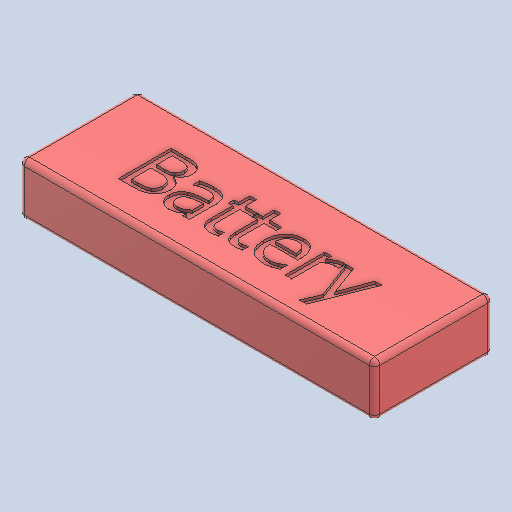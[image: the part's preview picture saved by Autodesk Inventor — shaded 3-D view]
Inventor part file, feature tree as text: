
AUTODESK INVENTOR PART (.ipt)
format: ipt  version: 2023 (Build 270158000, 158)  size: 488,448 bytes
history: native  units: in
note: dims shown in document units (in); Inventor stores cm internally (conversion verified against a paired STEP export)
features: extrude x2, sketch x2, fillet x1
ambient origin geometry x8: Origin, YZ Plane, XZ Plane, XY Plane, X Axis, Y Axis, Z Axis, Center Point
bodies: Solid1 (feature_tree)
feature tree (5):
  extrude  "Extrusion1"  Depth=1.7717in
  extrude  "Extrusion2"  Depth=0.0787in TaperAngle=0.0deg
  fillet  "Fillet1"  Radius=0.0787in
  sketch  "Sketch1"  dims[d0=5.315in d1=1.7717in]
  sketch  "Sketch2"  dims[d2=0.7874in d3=0.0in d4=0.0394in d5=0.0in d6=0.0787in]
